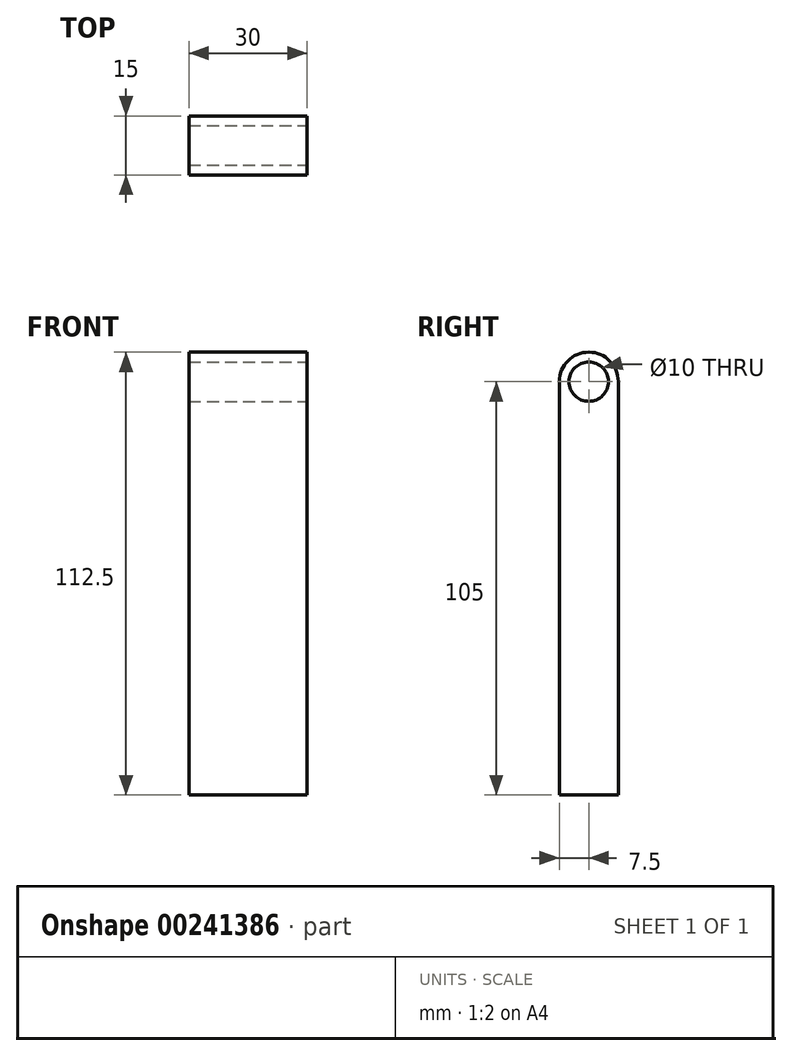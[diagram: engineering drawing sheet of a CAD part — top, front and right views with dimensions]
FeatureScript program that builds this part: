
annotation { "Feature Type Name" : "Feature", "Feature Type Description" : "" }
export const myFeature = defineFeature(function(context is Context, id is Id, definition is map)
    precondition{}
    {
        {
            var Q0;
            Q0=qCreatedBy(makeId("Right.planeOp"),FACE);
            var sketch = newSketch(context, id + "F0", { "sketchPlane" : qUnion([Q0])});
            skLineSegment(sketch, "E0.bottom", {"start": v(-7.5, 52.5) * mm, "end": v(7.5, 52.5) * mm});
            skLineSegment(sketch, "E0.top", {"start": v(-7.5, -52.5) * mm, "end": v(7.5, -52.5) * mm});
            skLineSegment(sketch, "E0.left", {"start": v(-7.5, 52.5) * mm, "end": v(-7.5, -52.5) * mm});
            skLineSegment(sketch, "E0.right", {"start": v(7.5, 52.5) * mm, "end": v(7.5, -52.5) * mm});
            skPoint(sketch, "E0.middle", {"position": v(0, 0) * mm});
            skCircle(sketch, "E1", {"center": v(0, 52.5) * mm, "radius": 7.5 * mm});
            skSolve(sketch);
        }
        {
            var Q0;
            Q0 = qSketchRegion(id + "F0", true);
            extrude(context, id + "F1", {"entities" : qUnion([Q0]), "depth" : 30 * mm});
        }
        {
            var Q0;
            Q0=makeQuery(id+"F1.opExtrude","CAP_FACE",FACE,{"disambiguationData":[OSD([sQuery(id+"F0.wireOp",EDGE,"E0.top"),sQuery(id+"F0.wireOp",EDGE,"E0.left"),sQuery(id+"F0.wireOp",EDGE,"E0.right"),sQuery(id+"F0.wireOp",EDGE,"E1")])],"isStart":false});
            var sketch = newSketch(context, id + "F2", { "sketchPlane" : qUnion([Q0])});
            skCircle(sketch, "E2", {"center": v(0, 52.5) * mm, "radius": 5 * mm});
            skSolve(sketch);
        }
        {
            var Q0;
            Q0 = qSketchRegion(id + "F2", true);
            extrude(context, id + "F3", {"entities" : qUnion([Q0]), "operationType" : NewBodyOperationType.REMOVE, "endBound" : BoundingType.THROUGH_ALL, "oppositeDirection" : true, "depth" : 25 * mm});
        }
    });
